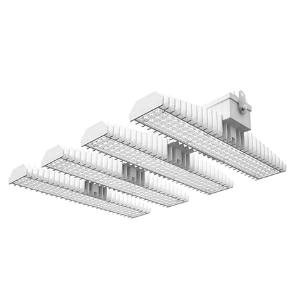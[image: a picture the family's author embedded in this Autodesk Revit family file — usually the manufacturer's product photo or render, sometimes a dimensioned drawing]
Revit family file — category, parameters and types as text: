
# Revit family: 3f_filippi_-_3f_lem_ho_medio_3f_filippi_-_58985_a0811_-_3f_lem_4_ho_led_280_dali_cr_medio___vt_91a7
name_source: partatom
category: Lighting Fixtures
units: mm (PartAtom-declared; Revit-internal decimal feet)

## family parameters
Cut with Voids When Loaded = No
Host = Face
Light Source = No
Part Type = Normal
Room Calculation Point = No
Round Connector Dimension = Use Diameter
Shared = No

## types (1)
- 3F Filippi - 3F LEM HO Medio (1 x LED, 41194 lm, 276 W, 4000 K)
    Apparent Load = 276 VA
    Approval mark = CE
    CIE Flux Codes = 83 96 99 100 100
    Color Rendering = 80
    Color Temperature = 4000 K
    Control Gear = Electronic transformer
    Default Elevation = 1800 mm
    Description = Industrial luminaire with high light output and high luminous efficiency designed with the most innovative technologies for environments with temperature up to 55°C.

ILLUMINOTECHNICAL
Luminous efficiency 100% (DLOR 99%, ULOR 1%).
Initial luminous flux of the luminaire 41194 lm.
Medium distribution with rectangular shape.
Installation Interdistance Transv.D = 1.02 x hu - Long.D = 1.06 x hu.
Tabular UGR (CIE 117 - 4H-8H; S=0.25H; 70/50/20): RUG 19.9 - 19.5.
Beam angle: 65° - 67°.
Luminous efficacy 149 lm/W.
Lifetime (L93/B10): 30000 h. (tq+25°C)
Lifetime (L90/B10): 50000 h. (tq+25°C)
Lifetime (L85/B10): 80000 h. (tq+25°C)
Lifetime (L80/B10): 100000 h. (tq+25°C)
Lifetime (L85/B10): 50000 h. (tq+55°C)
Sudden decreased luminous flux after 50000 hours: 0% (C0).
Photobiological safety in compliance with IEC/TR 62778: RG0 risk exempt, (IEC 62471).
In compliance with IEC/EN 62722-2-1 - IEC/EN 62717 standards.

SOURCE
4 Mid-Power linear LED modules 70W/840.
Energy efficiency class (UE 2019/2020 - UE 2019/2015): C.
CIE 13.3 Colour rendering index: CRI >80 (R9 <50%).
IES TM-30 Fidelity Index: Rf = 84 Rg = 95.
CCT nominal colour temperature 4000 K.
Colour initial tolerance (MacAdam): SDCM 3.

MECHANICAL
Passive modular heatsinks in die-casted aluminium, painted in white colour.
To optimize the thermal management of the LED module, the heatsinks are oversized and provided with self-cleaning of cooling fins.
Wiring body in aluminium and galvanised steel anchored solidly to the sinks and thermally separated.
3F Lens lenses with high luminous efficiency, transparent methacrylate (PMMA), fixed to the LED modules.
Fixing brackets in stainless steel.
Luminaire with limited surface temperature. - D - (EN 60598-2-24)
Dimensions: 757x542 mm, height 133 mm. Weight 19.788 kg.
IP65 protection degree.
Mechanical strength to impacts IK06 (1 joule).
Glow-wire test resistance 650°C.

ELECTRICAL
Halogen Free DALI-2 DATI (Parts 251, 252, 253), PUSH-DIM, electronic wiring 230V-50/60Hz, power factor 0.97 at full load, THD <25%, constant output current, class I, 2 driver, 2 DALI addresses.
Power of the luminaire 276 W.
ENEC - CE.
SAFE FLICKER: PstLM=<1 and SVM=<0.4 (IEC TR 61547-1 and IEC TR 63158), to ensure a more comfortable and safe light.
Luminaire compliant with EN 60598-2-22 for power supply from a centralised emergency system CPSS (Central Power Supply System), not incorporated in the luminaire - high risk areas excluded. The default power and flux are 100% in AC and 15% in DC.
Ambient temperature from -30°C to +55°C.
Temperature class T6 max 85°C.
Quick connection via M25 5P connector with 9-13 mm tightening range.
Power unit positioned on a separate compartment by the LED module to ensure optimum temperatures of cabling components, to be inspectable and maintainable.
Relative humidity UR: <85%.

INSTALLATION
Ceiling / Suspended / Wall.
All accessories dedicated to this product are available on the Catalog and on our website www.3F-Filippi.com.

ACCESSORIES
A0811 - VT transparent glass, tempered, not flammable, with sealing gasket.
One required for each light module. The pack contains 10 pieces.

APPLICATIONS
In commercial environments, exhibition and industrial areas, stores, open areas.
Environments in which it is necessary a total protection against falling fragments (eg environments with foodstuffs or machines with moving parts or with extreme temperature changes), use luminaires with polycarbonate lenses.

LIGHT MANAGEMENT
Recommended minimum setting: 10%.
The luminaire, equipped with (DALI-2 DATI) driver, can be controlled manually with 3F Easy Dim technology or automatically/manually with wired or wireless DALI/D2D control systems.
The D2D driver guarantees interoperability with other devices with the same certification by making the following information available:
Device Data (Part 251), Energy Report (Part 252), Diagnosis & Maintenance (Part 253).
In electrical systems without a regulation system (manual or automatic) and DALI bus, a suitable jumper must be made on the DA-DA terminals of the appliance.

WARNING
Fixture not suitable for cold stores with an ambient temperature <0°C and/or relative humidity >85%.
Luminaire designed for disposal/recycling at end-of-life.
Replaceable (LED only) light source by a professional. Replaceable control gear by a professional.
    Height = 133 mm  [stored 0.436352 ft]
    Lamp = 1 x LED
    Lamp Light Flux = 41194 lm
    Lamp Power = 276 W
    Lamp count = 1
    Length = 757 mm
    Lifetime = 50000 h
    Luminous efficacy = 149 lm/W
    Manufacturer = 3F Filippi
    ModVariant = No
    Model = 3F Filippi - 58985+A0811 - 3F LEM 4 HO LED 280 DALI CR MEDIO + VT
    Mounting Place = Ceiling
    Mounting Type = Pendant
    Number of Poles = 1
    OnlyDefault = Yes
    Power Factor = 1
    Product Name = 3F Filippi - 3F LEM HO Medio
    Product group = pendant luminaire
    ProductGroupID = 9
    Protection Class = Protection class I
    Protection Degree = IP 65
    RLX_Detail_Level = 1
    RLX_Emergency_Light_Flux = 0 lm
    RLX_Emergency_Type = 0
    RLX_Emergency_Type_DB = No
    RlxData = <blob elided: 120489 chars, md5=7d6f184c>
    Socket = socket
    Standby Power = 0 W
    System Light Flux = 41194 lm
    System Power = 276 W
    Type Comments = Product without accessories
    Type Image = 3f_filippi_-_lem_4__a0811.jpg
    URL = http://relux.com
    VarID = ---
    Voltage = 0 V
    Weight = 0.00 kg
    Width = 542 mm

note: [stored X ft] marks values corroborated as IEEE doubles in the binary element streams (Revit-internal decimal feet)

## geometry (parser evidence)
native form markers: Blend x4, Sweep x11
no freeform markers — native parametric forms only
